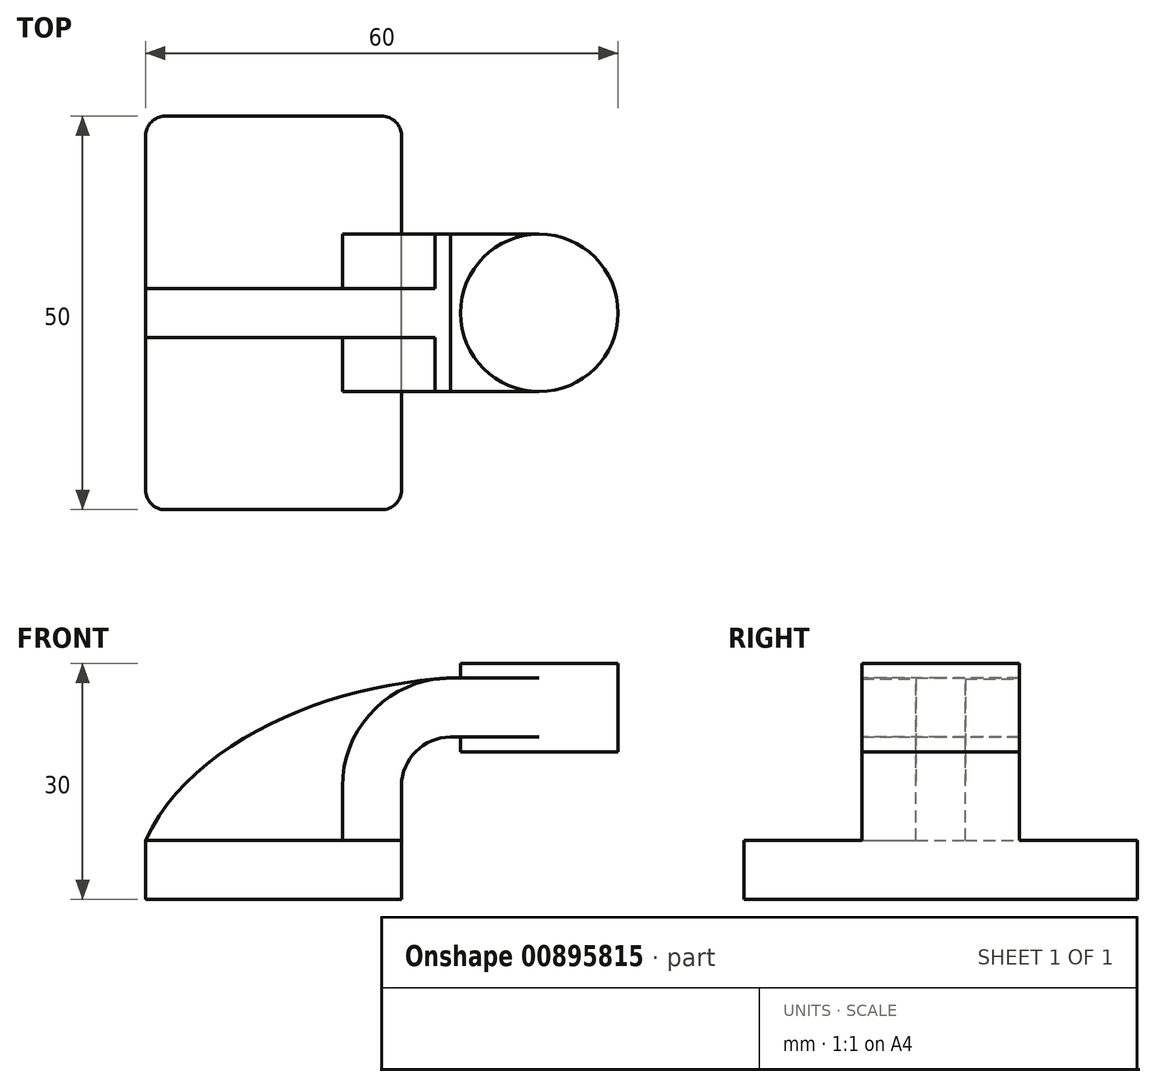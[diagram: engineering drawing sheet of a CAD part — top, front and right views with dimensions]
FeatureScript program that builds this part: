
annotation { "Feature Type Name" : "Feature", "Feature Type Description" : "" }
export const myFeature = defineFeature(function(context is Context, id is Id, definition is map)
    precondition{}
    {
        {
            var Q0;
            Q0=qCreatedBy(makeId("Front.planeOp"),FACE);
            var sketch = newSketch(context, id + "F0", { "sketchPlane" : qUnion([Q0])});
            skLineSegment(sketch, "E0.bottom", {"start": v(16.25, -3.75) * mm, "end": v(-16.25, -3.75) * mm});
            skLineSegment(sketch, "E0.top", {"start": v(16.25, 3.75) * mm, "end": v(-16.25, 3.75) * mm});
            skLineSegment(sketch, "E0.left", {"start": v(16.25, -3.75) * mm, "end": v(16.25, 3.75) * mm});
            skLineSegment(sketch, "E0.right", {"start": v(-16.25, -3.75) * mm, "end": v(-16.25, 3.75) * mm});
            skPoint(sketch, "E0.middle", {"position": v(0, 0) * mm});
            skLineSegment(sketch, "E1", {"start": v(16.25, 3.75) * mm, "end": v(16.25, 10.63) * mm});
            skArc(sketch, "E2", {"start": v(16.25, 10.63) * mm, "mid": v(18.08, 15.05) * mm, "end": v(22.5, 16.88) * mm});
            skLineSegment(sketch, "E3", {"start": v(22.5, 16.88) * mm, "end": v(33.75, 16.88) * mm});
            skLineSegment(sketch, "E4.bottom", {"start": v(43.75, 15) * mm, "end": v(23.75, 15) * mm});
            skLineSegment(sketch, "E4.top", {"start": v(43.75, 26.25) * mm, "end": v(23.75, 26.25) * mm});
            skLineSegment(sketch, "E4.left", {"start": v(43.75, 15) * mm, "end": v(43.75, 26.25) * mm});
            skLineSegment(sketch, "E4.right", {"start": v(23.75, 15) * mm, "end": v(23.75, 26.25) * mm});
            skPoint(sketch, "E4.middle", {"position": v(33.75, 20.63) * mm});
            skLineSegment(sketch, "E5.0", {"start": v(22.5, 24.38) * mm, "end": v(33.75, 24.38) * mm});
            skArc(sketch, "E5.1", {"start": v(8.75, 10.63) * mm, "mid": v(12.78, 20.35) * mm, "end": v(22.5, 24.38) * mm});
            skLineSegment(sketch, "E5.2", {"start": v(8.75, 3.75) * mm, "end": v(8.75, 10.63) * mm});
            skLineSegment(sketch, "E6", {"start": v(33.75, 15) * mm, "end": v(33.75, 26.25) * mm});
            skFitSpline(sketch, "E7", {"points": [v(-16.25, 3.75) * mm, v(22.5, 24.38) * mm], "startDerivative": vector(17.92, 38.6) * mm, "endDerivative": vector(45.87, 2.55) * mm});
            skSolve(sketch);
        }
        {
            var Q0;
            Q0=makeQuery(id+"F0.imprint","IMPRINT",FACE,{"disambiguationData":[TD([[makeQuery(id+"F0.imprint","IMPRINT",EDGE,{"derivedFrom":sQuery(id+"F0.wireOp",EDGE,"E0.bottom")}),-1.0]])]});
            extrude(context, id + "F1", {"entities" : qUnion([Q0]), "endBound" : BoundingType.SYMMETRIC, "depth" : 50 * mm, "offsetDistance" : 25 * mm});
        }
        {
            var Q0;
            {var subQ0=sQuery(id+"F0.wireOp",EDGE,"E6");var subQ1=sQuery(id+"F0.wireOp",EDGE,"E3");var subQ2=makeQuery(id+"F0.imprint","INTERSECT",VERTEX,{"derivedFrom":[subQ1,subQ0]});Q0=makeQuery(id+"F0.imprint","IMPRINT",FACE,{"disambiguationData":[TD([[makeQuery(id+"F0.imprint","IMPRINT",EDGE,{"disambiguationData":[TD([[subQ2,1.0]])],"derivedFrom":subQ1}),1.0]])]});}
            var Q1;
            {var subQ4=sQuery(id+"F0.wireOp",EDGE,"E1");Q1=makeQuery(id+"F0.imprint","IMPRINT",FACE,{"disambiguationData":[TD([[makeQuery(id+"F0.imprint","IMPRINT",EDGE,{"derivedFrom":subQ4}),1.0]])]});}
            extrude(context, id + "F2", {"entities" : qUnion([Q0, Q1]), "operationType" : NewBodyOperationType.ADD, "endBound" : BoundingType.SYMMETRIC, "depth" : 20 * mm, "offsetDistance" : 25 * mm});
        }
        {
            var Q0;
            {var subQ3=sQuery(id+"F0.wireOp",EDGE,"E5.2");Q0=makeQuery(id+"F0.imprint","IMPRINT",FACE,{"disambiguationData":[TD([[makeQuery(id+"F0.imprint","IMPRINT",EDGE,{"derivedFrom":subQ3}),1.0]])]});}
            extrude(context, id + "F3", {"entities" : qUnion([Q0]), "operationType" : NewBodyOperationType.ADD, "endBound" : BoundingType.SYMMETRIC, "depth" : 6.25 * mm, "offsetDistance" : 25 * mm});
        }
        {
            var Q0;
            {var subQ4=sQuery(id+"F0.wireOp",EDGE,"E4.left");Q0=makeQuery(id+"F0.imprint","IMPRINT",FACE,{"disambiguationData":[TD([[makeQuery(id+"F0.imprint","IMPRINT",EDGE,{"derivedFrom":subQ4}),1.0]])]});}
            var Q1;
            Q1=sQuery(id+"F0.wireOp",EDGE,"E6");
            revolve(context, id + "F4", {"operationType" : NewBodyOperationType.ADD, "surfaceOperationType" : NewSurfaceOperationType.NEW, "entities" : qUnion([Q0]), "axis" : qUnion([Q1]), "revolveType" : RevolveType.FULL});
        }
        {
            var Q0;
            Q0=makeQuery(id+"F1.opExtrude","CAP_EDGE",EDGE,{"disambiguationData":[OSD([sQuery(id+"F0.wireOp",EDGE,"E0.left")])],"isStart":false});
            var Q1;
            Q1=makeQuery(id+"F1.opExtrude","CAP_EDGE",EDGE,{"disambiguationData":[OSD([sQuery(id+"F0.wireOp",EDGE,"E0.right")])],"isStart":false});
            var Q2;
            Q2=makeQuery(id+"F1.opExtrude","CAP_EDGE",EDGE,{"disambiguationData":[OSD([sQuery(id+"F0.wireOp",EDGE,"E0.left")])],"isStart":true});
            var Q3;
            Q3=makeQuery(id+"F1.opExtrude","CAP_EDGE",EDGE,{"disambiguationData":[OSD([sQuery(id+"F0.wireOp",EDGE,"E0.right")])],"isStart":true});
            fillet(context, id + "F5", {"entities" : qUnion([Q0, Q1, Q2, Q3]), "radius" : 2.5 * mm, "tangentPropagation" : true, "allowEdgeOverflow" : false});
        }
    });
